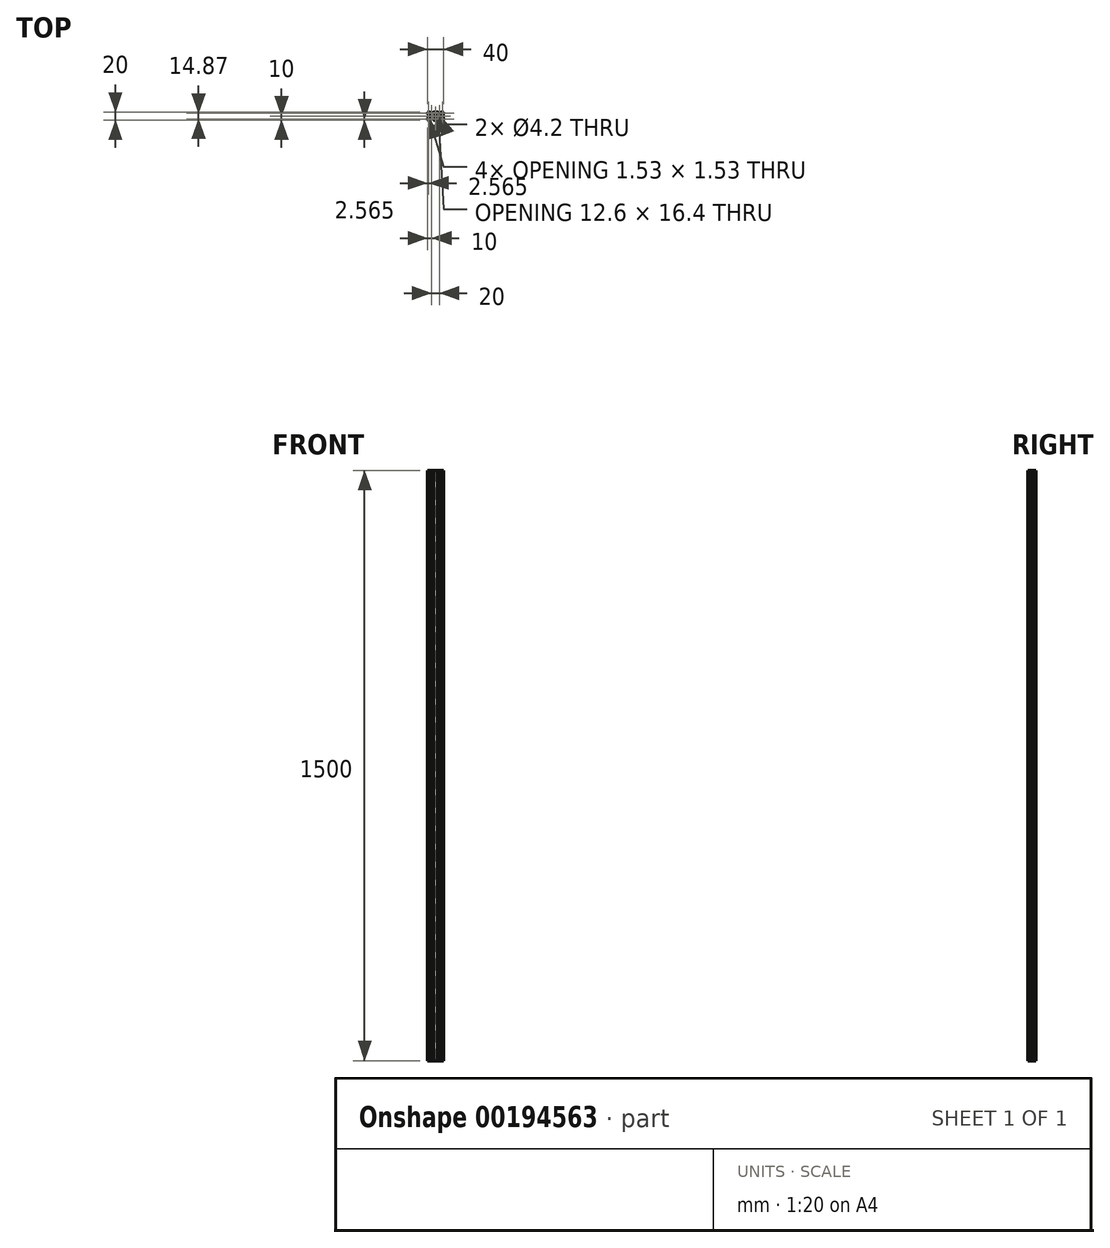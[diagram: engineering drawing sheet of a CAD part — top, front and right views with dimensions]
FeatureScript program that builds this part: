
annotation { "Feature Type Name" : "Feature", "Feature Type Description" : "" }
export const myFeature = defineFeature(function(context is Context, id is Id, definition is map)
    precondition{}
    {
        {
            var Q0;
            Q0=qCreatedBy(makeId("Top.planeOp"),FACE);
            var sketch = newSketch(context, id + "F0", { "sketchPlane" : qUnion([Q0])});
            skLineSegment(sketch, "E0.bottom", {"start": v(0, 0) * mm, "end": v(5.2, 0) * mm});
            skLineSegment(sketch, "E0.top", {"start": v(0, 20) * mm, "end": v(5.2, 20) * mm});
            skLineSegment(sketch, "E0.left", {"start": v(0, 0) * mm, "end": v(0, 5.2) * mm});
            skLineSegment(sketch, "E0.right", {"start": v(40, 0) * mm, "end": v(40, 5.2) * mm});
            skLineSegment(sketch, "E1", {"start": v(33.8, 12.84) * mm, "end": v(33.8, 7.16) * mm});
            skLineSegment(sketch, "E2", {"start": v(33.8, 12.84) * mm, "end": v(36.56, 15.6) * mm});
            skLineSegment(sketch, "E3", {"start": v(33.8, 7.16) * mm, "end": v(36.56, 4.4) * mm});
            skLineSegment(sketch, "E4", {"start": v(36.56, 15.6) * mm, "end": v(38.2, 15.6) * mm});
            skLineSegment(sketch, "E5", {"start": v(36.56, 4.4) * mm, "end": v(38.2, 4.4) * mm});
            skLineSegment(sketch, "E6", {"start": v(38.2, 13) * mm, "end": v(38.2, 15.6) * mm});
            skLineSegment(sketch, "E7", {"start": v(38.2, 7) * mm, "end": v(38.2, 4.4) * mm});
            skLineSegment(sketch, "E8.trimOffspring", {"start": v(40, 14.8) * mm, "end": v(40, 20) * mm});
            skLineSegment(sketch, "E9", {"start": v(33, 18.2) * mm, "end": v(35.6, 18.2) * mm});
            skLineSegment(sketch, "E10", {"start": v(35.6, 18.2) * mm, "end": v(35.6, 16.56) * mm});
            skLineSegment(sketch, "E11", {"start": v(35.6, 16.56) * mm, "end": v(32.84, 13.8) * mm});
            skLineSegment(sketch, "E12", {"start": v(32.84, 13.8) * mm, "end": v(27.16, 13.8) * mm});
            skLineSegment(sketch, "E13", {"start": v(27, 18.2) * mm, "end": v(24.4, 18.2) * mm});
            skLineSegment(sketch, "E14", {"start": v(24.4, 18.2) * mm, "end": v(24.4, 16.56) * mm});
            skLineSegment(sketch, "E15", {"start": v(24.4, 16.56) * mm, "end": v(27.16, 13.8) * mm});
            skLineSegment(sketch, "E16", {"start": v(33, 1.8) * mm, "end": v(35.6, 1.8) * mm});
            skLineSegment(sketch, "E17", {"start": v(35.6, 1.8) * mm, "end": v(35.6, 3.44) * mm});
            skLineSegment(sketch, "E18", {"start": v(35.6, 3.44) * mm, "end": v(32.84, 6.2) * mm});
            skLineSegment(sketch, "E19", {"start": v(32.84, 6.2) * mm, "end": v(27.16, 6.2) * mm});
            skLineSegment(sketch, "E20", {"start": v(27.16, 6.2) * mm, "end": v(24.4, 3.44) * mm});
            skLineSegment(sketch, "E21", {"start": v(24.4, 3.44) * mm, "end": v(24.4, 1.8) * mm});
            skLineSegment(sketch, "E22", {"start": v(24.4, 1.8) * mm, "end": v(27, 1.8) * mm});
            skLineSegment(sketch, "E23.trimOffspring", {"start": v(34.8, 20) * mm, "end": v(40, 20) * mm});
            skLineSegment(sketch, "E24.trimOffspring", {"start": v(34.8, 0) * mm, "end": v(40, 0) * mm});
            skLineSegment(sketch, "E25", {"start": v(7, 18.2) * mm, "end": v(4.4, 18.2) * mm});
            skLineSegment(sketch, "E26", {"start": v(4.4, 18.2) * mm, "end": v(4.4, 16.56) * mm});
            skLineSegment(sketch, "E27", {"start": v(4.4, 16.56) * mm, "end": v(7.16, 13.8) * mm});
            skLineSegment(sketch, "E28", {"start": v(7.16, 13.8) * mm, "end": v(12.84, 13.8) * mm});
            skLineSegment(sketch, "E29", {"start": v(12.84, 13.8) * mm, "end": v(15.6, 16.56) * mm});
            skLineSegment(sketch, "E30", {"start": v(15.6, 16.56) * mm, "end": v(15.6, 18.2) * mm});
            skLineSegment(sketch, "E31", {"start": v(15.6, 18.2) * mm, "end": v(13, 18.2) * mm});
            skLineSegment(sketch, "E32", {"start": v(1.8, 13) * mm, "end": v(1.8, 15.6) * mm});
            skLineSegment(sketch, "E33", {"start": v(1.8, 15.6) * mm, "end": v(3.44, 15.6) * mm});
            skLineSegment(sketch, "E34", {"start": v(3.44, 15.6) * mm, "end": v(6.2, 12.84) * mm});
            skLineSegment(sketch, "E35", {"start": v(6.2, 12.84) * mm, "end": v(6.2, 7.16) * mm});
            skLineSegment(sketch, "E36", {"start": v(6.2, 7.16) * mm, "end": v(3.44, 4.4) * mm});
            skLineSegment(sketch, "E37", {"start": v(3.44, 4.4) * mm, "end": v(1.8, 4.4) * mm});
            skLineSegment(sketch, "E38", {"start": v(1.8, 7) * mm, "end": v(1.8, 4.4) * mm});
            skLineSegment(sketch, "E39", {"start": v(7, 1.8) * mm, "end": v(4.4, 1.8) * mm});
            skLineSegment(sketch, "E40", {"start": v(4.4, 1.8) * mm, "end": v(4.4, 3.44) * mm});
            skLineSegment(sketch, "E41", {"start": v(4.4, 3.44) * mm, "end": v(7.16, 6.2) * mm});
            skLineSegment(sketch, "E42", {"start": v(7.16, 6.2) * mm, "end": v(12.84, 6.2) * mm});
            skLineSegment(sketch, "E43", {"start": v(12.84, 6.2) * mm, "end": v(15.6, 3.44) * mm});
            skLineSegment(sketch, "E44", {"start": v(15.6, 3.44) * mm, "end": v(15.6, 1.8) * mm});
            skLineSegment(sketch, "E45", {"start": v(15.6, 1.8) * mm, "end": v(13, 1.8) * mm});
            skLineSegment(sketch, "E46.trimOffspring", {"start": v(14.8, 20) * mm, "end": v(25.2, 20) * mm});
            skLineSegment(sketch, "E47.trimOffspring", {"start": v(0, 14.8) * mm, "end": v(0, 20) * mm});
            skLineSegment(sketch, "E48.trimOffspring", {"start": v(14.8, 0) * mm, "end": v(25.2, 0) * mm});
            skLineSegment(sketch, "E49", {"start": v(38.2, 7) * mm, "end": v(40, 5.2) * mm});
            skLineSegment(sketch, "E50", {"start": v(38.2, 13) * mm, "end": v(40, 14.8) * mm});
            skLineSegment(sketch, "E51", {"start": v(33, 1.8) * mm, "end": v(34.8, 0) * mm});
            skLineSegment(sketch, "E52", {"start": v(27, 1.8) * mm, "end": v(25.2, 0) * mm});
            skLineSegment(sketch, "E53", {"start": v(13, 1.8) * mm, "end": v(14.8, 0) * mm});
            skLineSegment(sketch, "E54", {"start": v(7, 1.8) * mm, "end": v(5.2, 0) * mm});
            skLineSegment(sketch, "E55", {"start": v(1.8, 7) * mm, "end": v(0, 5.2) * mm});
            skLineSegment(sketch, "E56", {"start": v(1.8, 13) * mm, "end": v(0, 14.8) * mm});
            skLineSegment(sketch, "E57", {"start": v(7, 18.2) * mm, "end": v(5.2, 20) * mm});
            skLineSegment(sketch, "E58", {"start": v(13, 18.2) * mm, "end": v(14.8, 20) * mm});
            skLineSegment(sketch, "E59", {"start": v(27, 18.2) * mm, "end": v(25.2, 20) * mm});
            skLineSegment(sketch, "E60", {"start": v(33, 18.2) * mm, "end": v(34.8, 20) * mm});
            skPoint(sketch, "E61.start.orphan", {"position": v(7, 0) * mm});
            skSolve(sketch);
        }
        {
            var Q0;
            Q0 = qSketchRegion(id + "F0", true);
            extrude(context, id + "F1", {"entities" : qUnion([Q0]), "depth" : 1500 * mm});
        }
        {
            var Q0;
            Q0=makeQuery(id+"F1.opExtrude","CAP_FACE",FACE,{"disambiguationData":[OSD([sQuery(id+"F0.wireOp",EDGE,"E0.bottom"),sQuery(id+"F0.wireOp",EDGE,"E0.top"),sQuery(id+"F0.wireOp",EDGE,"E0.left"),sQuery(id+"F0.wireOp",EDGE,"E0.right"),sQuery(id+"F0.wireOp",EDGE,"E1"),sQuery(id+"F0.wireOp",EDGE,"E2"),sQuery(id+"F0.wireOp",EDGE,"E3"),sQuery(id+"F0.wireOp",EDGE,"E4"),sQuery(id+"F0.wireOp",EDGE,"E5"),sQuery(id+"F0.wireOp",EDGE,"E6"),sQuery(id+"F0.wireOp",EDGE,"E7"),sQuery(id+"F0.wireOp",EDGE,"E8.trimOffspring"),sQuery(id+"F0.wireOp",EDGE,"E9"),sQuery(id+"F0.wireOp",EDGE,"E10"),sQuery(id+"F0.wireOp",EDGE,"E11"),sQuery(id+"F0.wireOp",EDGE,"E12"),sQuery(id+"F0.wireOp",EDGE,"E13"),sQuery(id+"F0.wireOp",EDGE,"E14"),sQuery(id+"F0.wireOp",EDGE,"E15"),sQuery(id+"F0.wireOp",EDGE,"E16"),sQuery(id+"F0.wireOp",EDGE,"E17"),sQuery(id+"F0.wireOp",EDGE,"E18"),sQuery(id+"F0.wireOp",EDGE,"E19"),sQuery(id+"F0.wireOp",EDGE,"E20"),sQuery(id+"F0.wireOp",EDGE,"E21"),sQuery(id+"F0.wireOp",EDGE,"E22"),sQuery(id+"F0.wireOp",EDGE,"E23.trimOffspring"),sQuery(id+"F0.wireOp",EDGE,"E24.trimOffspring"),sQuery(id+"F0.wireOp",EDGE,"E25"),sQuery(id+"F0.wireOp",EDGE,"E26"),sQuery(id+"F0.wireOp",EDGE,"E27"),sQuery(id+"F0.wireOp",EDGE,"E28"),sQuery(id+"F0.wireOp",EDGE,"E29"),sQuery(id+"F0.wireOp",EDGE,"E30"),sQuery(id+"F0.wireOp",EDGE,"E31"),sQuery(id+"F0.wireOp",EDGE,"E32"),sQuery(id+"F0.wireOp",EDGE,"E33"),sQuery(id+"F0.wireOp",EDGE,"E34"),sQuery(id+"F0.wireOp",EDGE,"E35"),sQuery(id+"F0.wireOp",EDGE,"E36"),sQuery(id+"F0.wireOp",EDGE,"E37"),sQuery(id+"F0.wireOp",EDGE,"E38"),sQuery(id+"F0.wireOp",EDGE,"E39"),sQuery(id+"F0.wireOp",EDGE,"E40"),sQuery(id+"F0.wireOp",EDGE,"E41"),sQuery(id+"F0.wireOp",EDGE,"E42"),sQuery(id+"F0.wireOp",EDGE,"E43"),sQuery(id+"F0.wireOp",EDGE,"E44"),sQuery(id+"F0.wireOp",EDGE,"E45"),sQuery(id+"F0.wireOp",EDGE,"E46.trimOffspring"),sQuery(id+"F0.wireOp",EDGE,"E47.trimOffspring"),sQuery(id+"F0.wireOp",EDGE,"E48.trimOffspring"),sQuery(id+"F0.wireOp",EDGE,"E49"),sQuery(id+"F0.wireOp",EDGE,"E50"),sQuery(id+"F0.wireOp",EDGE,"E51"),sQuery(id+"F0.wireOp",EDGE,"E52"),sQuery(id+"F0.wireOp",EDGE,"E53"),sQuery(id+"F0.wireOp",EDGE,"E54"),sQuery(id+"F0.wireOp",EDGE,"E55"),sQuery(id+"F0.wireOp",EDGE,"E56"),sQuery(id+"F0.wireOp",EDGE,"E57"),sQuery(id+"F0.wireOp",EDGE,"E58"),sQuery(id+"F0.wireOp",EDGE,"E59"),sQuery(id+"F0.wireOp",EDGE,"E60")])],"isStart":false});
            var sketch = newSketch(context, id + "F2", { "sketchPlane" : qUnion([Q0])});
            skLineSegment(sketch, "E62", {"start": v(1.8, 18.2) * mm, "end": v(1.8, 16.67) * mm});
            skLineSegment(sketch, "E63", {"start": v(1.8, 16.67) * mm, "end": v(3.33, 18.2) * mm});
            skLineSegment(sketch, "E64", {"start": v(3.33, 18.2) * mm, "end": v(1.8, 18.2) * mm});
            skLineSegment(sketch, "E65", {"start": v(1.8, 1.8) * mm, "end": v(3.33, 1.8) * mm});
            skLineSegment(sketch, "E66", {"start": v(3.33, 1.8) * mm, "end": v(1.8, 3.33) * mm});
            skLineSegment(sketch, "E67", {"start": v(1.8, 3.33) * mm, "end": v(1.8, 1.8) * mm});
            skLineSegment(sketch, "E68", {"start": v(38.2, 1.8) * mm, "end": v(38.2, 3.33) * mm});
            skLineSegment(sketch, "E69", {"start": v(38.2, 3.33) * mm, "end": v(36.67, 1.8) * mm});
            skLineSegment(sketch, "E70", {"start": v(36.67, 1.8) * mm, "end": v(38.2, 1.8) * mm});
            skLineSegment(sketch, "E71", {"start": v(38.2, 18.2) * mm, "end": v(38.2, 16.67) * mm});
            skLineSegment(sketch, "E72", {"start": v(38.2, 16.67) * mm, "end": v(36.67, 18.2) * mm});
            skLineSegment(sketch, "E73", {"start": v(36.67, 18.2) * mm, "end": v(38.2, 18.2) * mm});
            skSolve(sketch);
        }
        {
            var Q0;
            Q0 = qSketchRegion(id + "F2", true);
            extrude(context, id + "F3", {"entities" : qUnion([Q0]), "operationType" : NewBodyOperationType.REMOVE, "endBound" : BoundingType.THROUGH_ALL, "oppositeDirection" : true, "depth" : 25 * mm});
        }
        {
            var Q0;
            Q0=makeQuery(id+"F1.opExtrude","CAP_FACE",FACE,{"disambiguationData":[OSD([sQuery(id+"F0.wireOp",EDGE,"E0.bottom"),sQuery(id+"F0.wireOp",EDGE,"E0.top"),sQuery(id+"F0.wireOp",EDGE,"E0.left"),sQuery(id+"F0.wireOp",EDGE,"E0.right"),sQuery(id+"F0.wireOp",EDGE,"E1"),sQuery(id+"F0.wireOp",EDGE,"E2"),sQuery(id+"F0.wireOp",EDGE,"E3"),sQuery(id+"F0.wireOp",EDGE,"E4"),sQuery(id+"F0.wireOp",EDGE,"E5"),sQuery(id+"F0.wireOp",EDGE,"E6"),sQuery(id+"F0.wireOp",EDGE,"E7"),sQuery(id+"F0.wireOp",EDGE,"E8.trimOffspring"),sQuery(id+"F0.wireOp",EDGE,"E9"),sQuery(id+"F0.wireOp",EDGE,"E10"),sQuery(id+"F0.wireOp",EDGE,"E11"),sQuery(id+"F0.wireOp",EDGE,"E12"),sQuery(id+"F0.wireOp",EDGE,"E13"),sQuery(id+"F0.wireOp",EDGE,"E14"),sQuery(id+"F0.wireOp",EDGE,"E15"),sQuery(id+"F0.wireOp",EDGE,"E16"),sQuery(id+"F0.wireOp",EDGE,"E17"),sQuery(id+"F0.wireOp",EDGE,"E18"),sQuery(id+"F0.wireOp",EDGE,"E19"),sQuery(id+"F0.wireOp",EDGE,"E20"),sQuery(id+"F0.wireOp",EDGE,"E21"),sQuery(id+"F0.wireOp",EDGE,"E22"),sQuery(id+"F0.wireOp",EDGE,"E23.trimOffspring"),sQuery(id+"F0.wireOp",EDGE,"E24.trimOffspring"),sQuery(id+"F0.wireOp",EDGE,"E25"),sQuery(id+"F0.wireOp",EDGE,"E26"),sQuery(id+"F0.wireOp",EDGE,"E27"),sQuery(id+"F0.wireOp",EDGE,"E28"),sQuery(id+"F0.wireOp",EDGE,"E29"),sQuery(id+"F0.wireOp",EDGE,"E30"),sQuery(id+"F0.wireOp",EDGE,"E31"),sQuery(id+"F0.wireOp",EDGE,"E32"),sQuery(id+"F0.wireOp",EDGE,"E33"),sQuery(id+"F0.wireOp",EDGE,"E34"),sQuery(id+"F0.wireOp",EDGE,"E35"),sQuery(id+"F0.wireOp",EDGE,"E36"),sQuery(id+"F0.wireOp",EDGE,"E37"),sQuery(id+"F0.wireOp",EDGE,"E38"),sQuery(id+"F0.wireOp",EDGE,"E39"),sQuery(id+"F0.wireOp",EDGE,"E40"),sQuery(id+"F0.wireOp",EDGE,"E41"),sQuery(id+"F0.wireOp",EDGE,"E42"),sQuery(id+"F0.wireOp",EDGE,"E43"),sQuery(id+"F0.wireOp",EDGE,"E44"),sQuery(id+"F0.wireOp",EDGE,"E45"),sQuery(id+"F0.wireOp",EDGE,"E46.trimOffspring"),sQuery(id+"F0.wireOp",EDGE,"E47.trimOffspring"),sQuery(id+"F0.wireOp",EDGE,"E48.trimOffspring"),sQuery(id+"F0.wireOp",EDGE,"E49"),sQuery(id+"F0.wireOp",EDGE,"E50"),sQuery(id+"F0.wireOp",EDGE,"E51"),sQuery(id+"F0.wireOp",EDGE,"E52"),sQuery(id+"F0.wireOp",EDGE,"E53"),sQuery(id+"F0.wireOp",EDGE,"E54"),sQuery(id+"F0.wireOp",EDGE,"E55"),sQuery(id+"F0.wireOp",EDGE,"E56"),sQuery(id+"F0.wireOp",EDGE,"E57"),sQuery(id+"F0.wireOp",EDGE,"E58"),sQuery(id+"F0.wireOp",EDGE,"E59"),sQuery(id+"F0.wireOp",EDGE,"E60")])],"isStart":false});
            var sketch = newSketch(context, id + "F4", { "sketchPlane" : qUnion([Q0])});
            skLineSegment(sketch, "E74", {"start": v(17.1, 18.2) * mm, "end": v(22.9, 18.2) * mm});
            skLineSegment(sketch, "E75", {"start": v(22.9, 1.8) * mm, "end": v(17.1, 1.8) * mm});
            skLineSegment(sketch, "E76", {"start": v(17.1, 1.8) * mm, "end": v(17.1, 3.76) * mm});
            skLineSegment(sketch, "E77", {"start": v(22.9, 1.8) * mm, "end": v(22.9, 3.76) * mm});
            skLineSegment(sketch, "E78", {"start": v(22.9, 18.2) * mm, "end": v(22.9, 16.24) * mm});
            skLineSegment(sketch, "E79", {"start": v(17.1, 18.2) * mm, "end": v(17.1, 16.24) * mm});
            skLineSegment(sketch, "E80", {"start": v(22.9, 16.24) * mm, "end": v(26.3, 12.84) * mm});
            skLineSegment(sketch, "E81", {"start": v(26.3, 12.84) * mm, "end": v(26.3, 7.16) * mm});
            skLineSegment(sketch, "E82", {"start": v(26.3, 7.16) * mm, "end": v(22.9, 3.76) * mm});
            skLineSegment(sketch, "E83", {"start": v(17.1, 3.76) * mm, "end": v(13.7, 7.16) * mm});
            skLineSegment(sketch, "E84", {"start": v(13.7, 7.16) * mm, "end": v(13.7, 12.84) * mm});
            skLineSegment(sketch, "E85", {"start": v(13.7, 12.84) * mm, "end": v(17.1, 16.24) * mm});
            skCircle(sketch, "E86", {"center": v(30, 10) * mm, "radius": 2.1 * mm});
            skPoint(sketch, "E86.centerSnap0", {"position": v(30, 13.8) * mm});
            skPoint(sketch, "E86.centerSnap1", {"position": v(26.3, 10) * mm});
            skCircle(sketch, "E87", {"center": v(10, 10) * mm, "radius": 2.1 * mm});
            skPoint(sketch, "E87.centerSnap0", {"position": v(10, 13.8) * mm});
            skPoint(sketch, "E87.centerSnap1", {"position": v(13.7, 10) * mm});
            skSolve(sketch);
        }
        {
            var Q0;
            Q0 = qSketchRegion(id + "F4", true);
            extrude(context, id + "F5", {"entities" : qUnion([Q0]), "operationType" : NewBodyOperationType.REMOVE, "endBound" : BoundingType.THROUGH_ALL, "oppositeDirection" : true, "depth" : 25 * mm});
        }
    });
